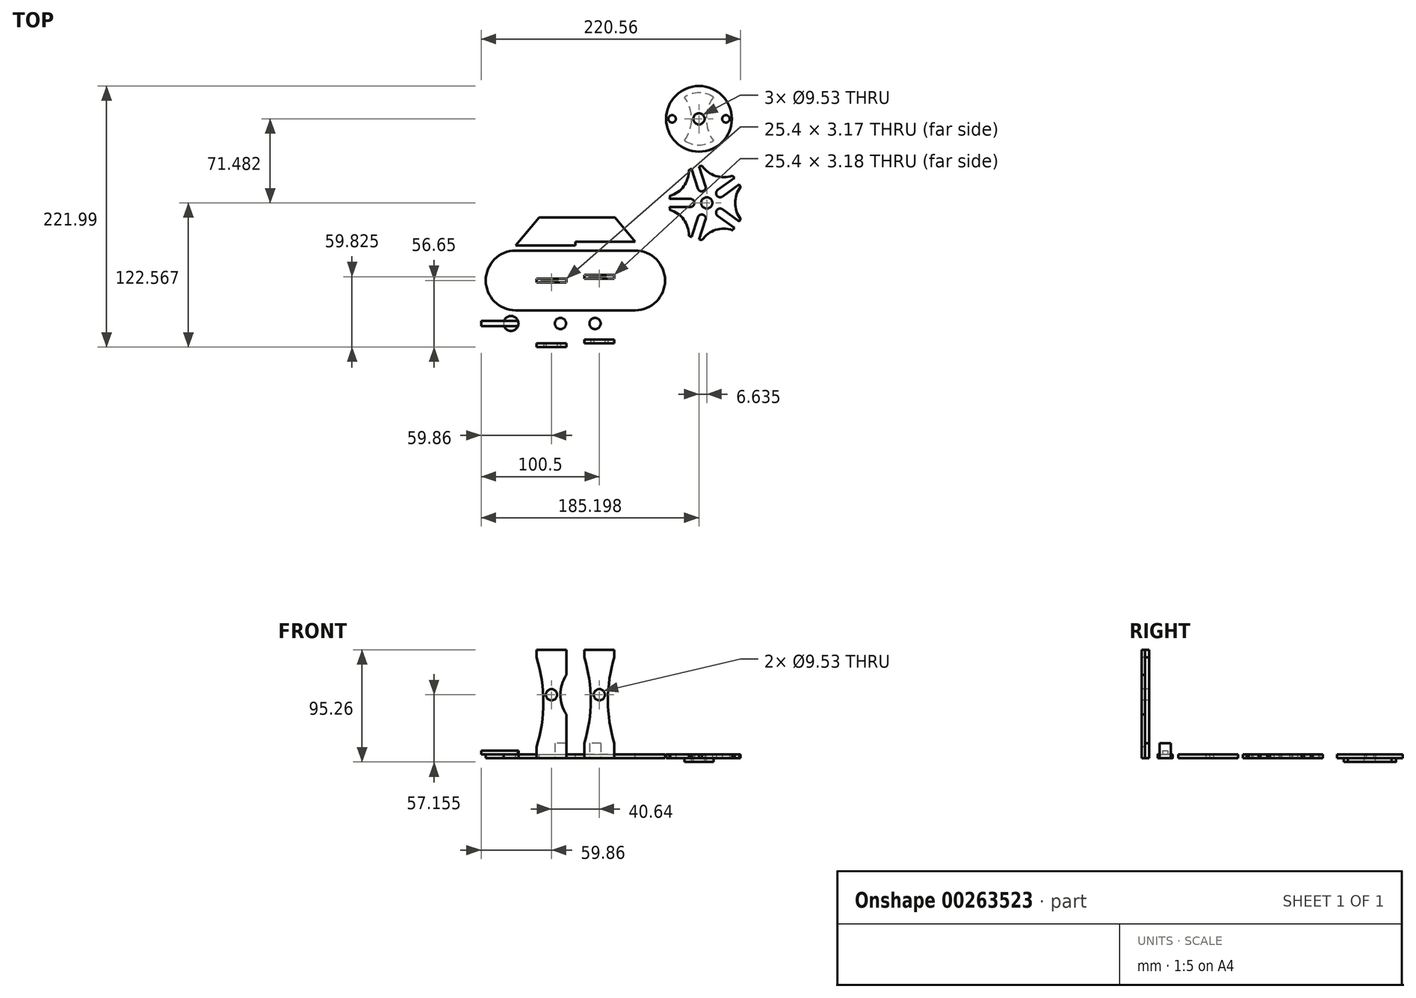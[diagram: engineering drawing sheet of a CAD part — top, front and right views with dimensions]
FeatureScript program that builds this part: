
annotation { "Feature Type Name" : "Feature", "Feature Type Description" : "" }
export const myFeature = defineFeature(function(context is Context, id is Id, definition is map)
    precondition{}
    {
        {
            var Q0;
            Q0=qCreatedBy(makeId("Top.planeOp"),FACE);
            var sketch = newSketch(context, id + "F0", { "sketchPlane" : qUnion([Q0])});
            skArc(sketch, "E0", {"start": v(-38.1, 25.4) * mm, "mid": v(-63.5, 0) * mm, "end": v(-38.1, -25.4) * mm});
            skArc(sketch, "E1", {"start": v(63.5, -25.4) * mm, "mid": v(88.9, 0) * mm, "end": v(63.5, 25.4) * mm});
            skLineSegment(sketch, "E2", {"start": v(-38.1, 25.4) * mm, "end": v(63.5, 25.4) * mm});
            skLineSegment(sketch, "E3", {"start": v(-38.1, -25.4) * mm, "end": v(63.5, -25.4) * mm});
            skSolve(sketch);
        }
        {
            var Q0;
            Q0=makeQuery(id+"F0.imprint","IMPRINT",FACE,{"disambiguationData":[TD([[makeQuery(id+"F0.imprint","IMPRINT",EDGE,{"derivedFrom":sQuery(id+"F0.wireOp",EDGE,"E0")}),1.0]])]});
            extrude(context, id + "F1", {"entities" : qUnion([Q0]), "depth" : 3.17 * mm});
        }
        {
            var Q0;
            Q0=qCreatedBy(makeId("Top.planeOp"),FACE);
            var sketch = newSketch(context, id + "F2", { "sketchPlane" : qUnion([Q0])});
            skCircle(sketch, "E4", {"center": v(117.72, 137.4) * mm, "radius": 27.94 * mm});
            skArc(sketch, "E5", {"start": v(130.02, 155.9) * mm, "mid": v(117.72, 159.62) * mm, "end": v(105.42, 155.9) * mm});
            skArc(sketch, "E6", {"start": v(146.1, 42.78) * mm, "mid": v(147, 43.67) * mm, "end": v(147.87, 44.6) * mm});
            skArc(sketch, "E7", {"start": v(120.36, 97.42) * mm, "mid": v(131.8, 88.87) * mm, "end": v(146.1, 89.05) * mm});
            skArc(sketch, "E8", {"start": v(93.16, 71.85) * mm, "mid": v(104.83, 80.1) * mm, "end": v(109.07, 93.75) * mm});
            skArc(sketch, "E9", {"start": v(109.07, 38.09) * mm, "mid": v(104.83, 51.73) * mm, "end": v(93.16, 59.98) * mm});
            skArc(sketch, "E10", {"start": v(146.1, 42.78) * mm, "mid": v(131.8, 42.97) * mm, "end": v(120.36, 34.42) * mm});
            skArc(sketch, "E11.trimOffspring", {"start": v(109.07, 38.09) * mm, "mid": v(110.2, 37.5) * mm, "end": v(111.34, 36.96) * mm});
            skArc(sketch, "E12.trimOffspring", {"start": v(153.08, 79.45) * mm, "mid": v(152.51, 80.58) * mm, "end": v(151.9, 81.7) * mm});
            skArc(sketch, "E13.trimOffspring", {"start": v(93.16, 71.85) * mm, "mid": v(92.95, 70.6) * mm, "end": v(92.79, 69.35) * mm});
            skArc(sketch, "E14.trimOffspring", {"start": v(120.36, 97.42) * mm, "mid": v(119.1, 97.23) * mm, "end": v(117.86, 97) * mm});
            skPoint(sketch, "E15", {"position": v(170.7, 65.92) * mm});
            skArc(sketch, "E16", {"start": v(153.08, 79.45) * mm, "mid": v(148.48, 65.92) * mm, "end": v(153.08, 52.39) * mm});
            skPoint(sketch, "E17", {"position": v(92.6, 65.92) * mm});
            skPoint(sketch, "E18", {"position": v(114.54, 35.72) * mm});
            skPoint(sketch, "E19", {"position": v(150.04, 47.26) * mm});
            skPoint(sketch, "E20", {"position": v(150.04, 84.58) * mm});
            skPoint(sketch, "E21", {"position": v(114.54, 96.11) * mm});
            skCircle(sketch, "E22", {"center": v(94.86, 137.4) * mm, "radius": 3.18 * mm});
            skPoint(sketch, "E23", {"position": v(110.38, 65.92) * mm});
            skArc(sketch, "E24.trimOffspring", {"start": v(92.79, 62.49) * mm, "mid": v(92.95, 61.23) * mm, "end": v(93.16, 59.98) * mm});
            skArc(sketch, "E25.trimOffspring", {"start": v(111.34, 94.88) * mm, "mid": v(110.2, 94.33) * mm, "end": v(109.07, 93.75) * mm});
            skArc(sketch, "E26.trimOffspring", {"start": v(147.87, 87.24) * mm, "mid": v(147, 88.17) * mm, "end": v(146.1, 89.05) * mm});
            skArc(sketch, "E27.trimOffspring", {"start": v(151.9, 50.14) * mm, "mid": v(152.51, 51.25) * mm, "end": v(153.08, 52.39) * mm});
            skArc(sketch, "E28.trimOffspring", {"start": v(117.86, 34.84) * mm, "mid": v(119.1, 34.6) * mm, "end": v(120.36, 34.42) * mm});
            skCircle(sketch, "E29", {"center": v(124.35, 65.92) * mm, "radius": 4.76 * mm});
            skCircle(sketch, "E30", {"center": v(117.72, 137.4) * mm, "radius": 4.76 * mm});
            skCircle(sketch, "E31", {"center": v(140.58, 137.4) * mm, "radius": 3.18 * mm});
            skArc(sketch, "E32", {"start": v(130.02, 155.9) * mm, "mid": v(124.07, 137.4) * mm, "end": v(130.02, 118.9) * mm});
            skArc(sketch, "E33", {"start": v(105.42, 118.9) * mm, "mid": v(111.37, 137.4) * mm, "end": v(105.42, 155.9) * mm});
            skArc(sketch, "E34.trimOffspring", {"start": v(105.42, 118.9) * mm, "mid": v(117.72, 115.17) * mm, "end": v(130.02, 118.9) * mm});
            skPoint(sketch, "E35.end.orphan", {"position": v(110.38, 62.49) * mm});
            skPoint(sketch, "E35.start.orphan", {"position": v(110.38, 69.35) * mm});
            skPoint(sketch, "E36", {"position": v(93.16, 65.92) * mm});
            skArc(sketch, "E37", {"start": v(110.38, 69.35) * mm, "mid": v(113.81, 65.92) * mm, "end": v(110.38, 62.49) * mm});
            skLineSegment(sketch, "E38", {"start": v(110.38, 69.35) * mm, "end": v(92.79, 69.35) * mm});
            skLineSegment(sketch, "E39", {"start": v(110.38, 62.49) * mm, "end": v(92.79, 62.49) * mm});
            skLineSegment(sketch, "E40.1.0", {"start": v(123.3, 80.26) * mm, "end": v(117.86, 97) * mm});
            skArc(sketch, "E40.1.1", {"start": v(123.3, 80.26) * mm, "mid": v(121.1, 75.94) * mm, "end": v(116.78, 78.14) * mm});
            skLineSegment(sketch, "E40.1.2", {"start": v(116.78, 78.14) * mm, "end": v(111.34, 94.88) * mm});
            skLineSegment(sketch, "E40.2.0", {"start": v(137.67, 71.35) * mm, "end": v(151.9, 81.7) * mm});
            skArc(sketch, "E40.2.1", {"start": v(137.67, 71.35) * mm, "mid": v(132.88, 72.11) * mm, "end": v(133.64, 76.9) * mm});
            skLineSegment(sketch, "E40.2.2", {"start": v(133.64, 76.9) * mm, "end": v(147.87, 87.24) * mm});
            skLineSegment(sketch, "E40.3.0", {"start": v(133.64, 54.93) * mm, "end": v(147.87, 44.6) * mm});
            skArc(sketch, "E40.3.1", {"start": v(133.64, 54.93) * mm, "mid": v(132.88, 59.72) * mm, "end": v(137.67, 60.48) * mm});
            skLineSegment(sketch, "E40.3.2", {"start": v(137.67, 60.48) * mm, "end": v(151.9, 50.14) * mm});
            skLineSegment(sketch, "E40.4.0", {"start": v(116.78, 53.7) * mm, "end": v(111.34, 36.96) * mm});
            skArc(sketch, "E40.4.1", {"start": v(116.78, 53.7) * mm, "mid": v(121.1, 55.9) * mm, "end": v(123.3, 51.57) * mm});
            skLineSegment(sketch, "E40.4.2", {"start": v(123.3, 51.57) * mm, "end": v(117.86, 34.84) * mm});
            skLineSegment(sketch, "E40.anchor1", {"start": v(124.35, 65.92) * mm, "end": v(92.79, 69.35) * mm, "construction": true});
            skLineSegment(sketch, "E40.anchor2", {"start": v(124.35, 65.92) * mm, "end": v(111.34, 36.96) * mm, "construction": true});
            skSolve(sketch);
        }
        {
            var Q0;
            Q0=makeQuery(id+"F1.opExtrude","CAP_FACE",FACE,{"disambiguationData":[OSD([sQuery(id+"F0.wireOp",EDGE,"E0"),sQuery(id+"F0.wireOp",EDGE,"E1"),sQuery(id+"F0.wireOp",EDGE,"E2"),sQuery(id+"F0.wireOp",EDGE,"E3")])],"isStart":false});
            var sketch = newSketch(context, id + "F3", { "sketchPlane" : qUnion([Q0])});
            skSolve(sketch);
        }
        {
            var Q0;
            Q0=makeQuery(id+"F2.imprint","IMPRINT",FACE,{"disambiguationData":[TD([[makeQuery(id+"F2.imprint","IMPRINT",EDGE,{"derivedFrom":sQuery(id+"F2.wireOp",EDGE,"E6")}),1.0]])]});
            extrude(context, id + "F4", {"entities" : qUnion([Q0]), "depth" : 3.17 * mm});
        }
        {
            var Q0;
            Q0=makeQuery(id+"F2.imprint","IMPRINT",FACE,{"disambiguationData":[TD([[makeQuery(id+"F2.imprint","IMPRINT",EDGE,{"derivedFrom":sQuery(id+"F2.wireOp",EDGE,"E5")}),1.0]])]});
            extrude(context, id + "F5", {"entities" : qUnion([Q0]), "depth" : 3.17 * mm});
        }
        {
            var Q0;
            Q0=makeQuery(id+"F2.imprint","IMPRINT",FACE,{"disambiguationData":[TD([[makeQuery(id+"F2.imprint","IMPRINT",EDGE,{"derivedFrom":sQuery(id+"F2.wireOp",EDGE,"E4")}),1.0]])]});
            extrude(context, id + "F6", {"entities" : qUnion([Q0]), "operationType" : NewBodyOperationType.ADD, "depth" : 3.17 * mm});
        }
        {
            var Q0;
            Q0=makeQuery(id+"F3.imprint","IMPRINT",FACE,{"disambiguationData":[TD([[makeQuery(id+"F3.imprint","IMPRINT",EDGE,{"derivedFrom":makeQuery(id+"F1.opExtrude","CAP_EDGE",EDGE,{"disambiguationData":[OSD([sQuery(id+"F0.wireOp",EDGE,"E0")])],"isStart":false})}),1.0]])]});
            var sketch = newSketch(context, id + "F7", { "sketchPlane" : qUnion([Q0])});
            skPoint(sketch, "E41", {"position": v(-38.1, 53.47) * mm});
            skPoint(sketch, "E42", {"position": v(63.5, 53.47) * mm});
            skLineSegment(sketch, "E43", {"start": v(-18.12, 53.47) * mm, "end": v(46.18, 53.47) * mm});
            skPoint(sketch, "E44", {"position": v(12.7, 53.47) * mm});
            skPoint(sketch, "E45", {"position": v(12.7, 0) * mm});
            skPoint(sketch, "E46", {"position": v(-7.62, 0) * mm});
            skLineSegment(sketch, "E47.bottom", {"start": v(-20.32, -1.59) * mm, "end": v(5.08, -1.59) * mm});
            skLineSegment(sketch, "E47.left", {"start": v(-20.32, -1.59) * mm, "end": v(-20.32, 1.59) * mm});
            skLineSegment(sketch, "E47.right", {"start": v(5.08, -1.59) * mm, "end": v(5.08, 1.59) * mm});
            skLineSegment(sketch, "E48.top", {"start": v(20.32, 1.59) * mm, "end": v(45.72, 1.59) * mm});
            skLineSegment(sketch, "E49", {"start": v(20.32, 1.59) * mm, "end": v(20.32, 4.76) * mm});
            skLineSegment(sketch, "E50", {"start": v(20.32, 4.76) * mm, "end": v(45.72, 4.76) * mm});
            skLineSegment(sketch, "E51", {"start": v(45.72, 4.76) * mm, "end": v(45.72, 1.59) * mm});
            skPoint(sketch, "E52", {"position": v(33.02, 0) * mm});
            skLineSegment(sketch, "E53", {"start": v(-20.32, 1.59) * mm, "end": v(5.08, 1.59) * mm});
            skLineSegment(sketch, "E54", {"start": v(5.08, -53.47) * mm, "end": v(5.08, -56.65) * mm});
            skLineSegment(sketch, "E55", {"start": v(5.08, -56.65) * mm, "end": v(-20.32, -56.65) * mm});
            skLineSegment(sketch, "E56", {"start": v(-20.32, -56.65) * mm, "end": v(-20.32, -53.47) * mm});
            skLineSegment(sketch, "E57", {"start": v(-20.32, -53.47) * mm, "end": v(5.08, -53.47) * mm});
            skLineSegment(sketch, "E58", {"start": v(20.32, -53.47) * mm, "end": v(20.32, -50.3) * mm});
            skLineSegment(sketch, "E59", {"start": v(20.32, -50.3) * mm, "end": v(45.72, -50.3) * mm});
            skLineSegment(sketch, "E60", {"start": v(45.72, -50.3) * mm, "end": v(45.72, -53.47) * mm});
            skLineSegment(sketch, "E61", {"start": v(45.72, -53.47) * mm, "end": v(20.32, -53.47) * mm});
            skPoint(sketch, "E62", {"position": v(33.02, 4.76) * mm});
            skLineSegment(sketch, "E63", {"start": v(-38.1, 29.66) * mm, "end": v(12.7, 29.66) * mm});
            skLineSegment(sketch, "E64", {"start": v(63.5, 32.83) * mm, "end": v(12.7, 32.83) * mm});
            skLineSegment(sketch, "E65", {"start": v(12.7, 29.66) * mm, "end": v(12.7, 32.83) * mm});
            skLineSegment(sketch, "E66", {"start": v(-38.1, 29.66) * mm, "end": v(-18.12, 53.47) * mm});
            skLineSegment(sketch, "E67", {"start": v(63.5, 32.83) * mm, "end": v(46.18, 53.47) * mm});
            skSolve(sketch);
        }
        {
            var Q0;
            Q0=makeQuery(id+"F2.imprint","IMPRINT",FACE,{"disambiguationData":[TD([[makeQuery(id+"F2.imprint","IMPRINT",EDGE,{"derivedFrom":sQuery(id+"F2.wireOp",EDGE,"E6")}),1.0]])]});
            extrude(context, id + "F8", {"entities" : qUnion([Q0]), "operationType" : NewBodyOperationType.ADD, "depth" : 3.17 * mm});
        }
        {
            var Q0;
            Q0=makeQuery(id+"F7.imprint","IMPRINT",FACE,{"disambiguationData":[TD([[makeQuery(id+"F7.imprint","IMPRINT",EDGE,{"derivedFrom":sQuery(id+"F7.wireOp",EDGE,"E47.bottom")}),1.0]])]});
            extrude(context, id + "F9", {"entities" : qUnion([Q0]), "operationType" : NewBodyOperationType.REMOVE, "oppositeDirection" : true, "depth" : 3.17 * mm});
        }
        {
            var Q0;
            Q0=makeQuery(id+"F7.imprint","IMPRINT",FACE,{"disambiguationData":[TD([[makeQuery(id+"F7.imprint","IMPRINT",EDGE,{"derivedFrom":sQuery(id+"F7.wireOp",EDGE,"E48.top")}),1.0]])]});
            extrude(context, id + "F10", {"entities" : qUnion([Q0]), "operationType" : NewBodyOperationType.REMOVE, "oppositeDirection" : true, "depth" : 3.17 * mm});
        }
        {
            var Q0;
            Q0=makeQuery(id+"F7.imprint","IMPRINT",FACE,{"disambiguationData":[TD([[makeQuery(id+"F7.imprint","IMPRINT",EDGE,{"derivedFrom":sQuery(id+"F7.wireOp",EDGE,"E54")}),-1.0]])]});
            var Q1;
            Q1=makeQuery(id+"F7.imprint","IMPRINT",FACE,{"disambiguationData":[TD([[makeQuery(id+"F7.imprint","IMPRINT",EDGE,{"derivedFrom":sQuery(id+"F7.wireOp",EDGE,"E58")}),-1.0]])]});
            extrude(context, id + "F11", {"entities" : qUnion([Q0, Q1]), "depth" : 88.9 * mm});
        }
        {
            var Q0;
            Q0=makeQuery(id+"F11.opExtrude","SWEPT_FACE",FACE,{"disambiguationData":[OSD([sQuery(id+"F7.wireOp",EDGE,"E61")])]});
            var sketch = newSketch(context, id + "F12", { "sketchPlane" : qUnion([Q0])});
            skLineSegment(sketch, "E68", {"start": v(20.32, 6.35) * mm, "end": v(20.32, 12.7) * mm});
            skLineSegment(sketch, "E69", {"start": v(45.72, 12.7) * mm, "end": v(45.72, 6.35) * mm});
            skLineSegment(sketch, "E70", {"start": v(20.32, 92.08) * mm, "end": v(20.32, 85.73) * mm});
            skLineSegment(sketch, "E71", {"start": v(45.72, 92.08) * mm, "end": v(45.72, 85.73) * mm});
            skArc(sketch, "E72", {"start": v(20.32, 12.7) * mm, "mid": v(25.68, 49.21) * mm, "end": v(20.32, 85.73) * mm});
            skArc(sketch, "E73", {"start": v(45.72, 85.73) * mm, "mid": v(40.36, 49.21) * mm, "end": v(45.72, 12.7) * mm});
            skPoint(sketch, "E74", {"position": v(33.02, 92.08) * mm});
            skPoint(sketch, "E75", {"position": v(33.02, 53.98) * mm});
            skCircle(sketch, "E76", {"center": v(33.02, 53.98) * mm, "radius": 4.76 * mm});
            skSolve(sketch);
        }
        {
            var Q0;
            Q0=makeQuery(id+"F7.imprint","IMPRINT",FACE,{"disambiguationData":[TD([[makeQuery(id+"F7.imprint","IMPRINT",EDGE,{"derivedFrom":sQuery(id+"F7.wireOp",EDGE,"E54")}),-1.0]])]});
            extrude(context, id + "F13", {"entities" : qUnion([Q0]), "operationType" : NewBodyOperationType.ADD, "oppositeDirection" : true, "depth" : 3.17 * mm});
        }
        {
            var Q0;
            Q0=makeQuery(id+"F7.imprint","IMPRINT",FACE,{"disambiguationData":[TD([[makeQuery(id+"F7.imprint","IMPRINT",EDGE,{"derivedFrom":sQuery(id+"F7.wireOp",EDGE,"E58")}),-1.0]])]});
            extrude(context, id + "F14", {"entities" : qUnion([Q0]), "operationType" : NewBodyOperationType.ADD, "oppositeDirection" : true, "depth" : 3.17 * mm});
        }
        {
            var Q0;
            {var subQ0=sQuery(id+"F7.wireOp",EDGE,"E55");Q0=makeQuery(id+"F13.boolean.opBoolean","MERGE",FACE,{"derivedFrom":[makeQuery(id+"F11.opExtrude","SWEPT_FACE",FACE,{"disambiguationData":[OSD([subQ0])]}),makeQuery(id+"F13.opExtrude","SWEPT_FACE",FACE,{"disambiguationData":[OSD([subQ0])]})]});}
            var sketch = newSketch(context, id + "F15", { "sketchPlane" : qUnion([Q0])});
            skPoint(sketch, "E77", {"position": v(-7.62, 92.08) * mm});
            skPoint(sketch, "E78", {"position": v(-7.62, 53.98) * mm});
            skPoint(sketch, "E79", {"position": v(30.48, 53.98) * mm});
            skArc(sketch, "E80", {"start": v(5.08, 70.82) * mm, "mid": v(0, 53.98) * mm, "end": v(5.08, 37.13) * mm});
            skLineSegment(sketch, "E81", {"start": v(-20.32, 3.18) * mm, "end": v(-20.32, 9.53) * mm});
            skLineSegment(sketch, "E82", {"start": v(-20.32, 92.08) * mm, "end": v(-20.32, 85.73) * mm});
            skArc(sketch, "E83", {"start": v(-20.32, 9.53) * mm, "mid": v(-14.47, 47.63) * mm, "end": v(-20.32, 85.72) * mm});
            skCircle(sketch, "E84", {"center": v(-7.62, 53.98) * mm, "radius": 4.76 * mm});
            skSolve(sketch);
        }
        {
            var Q0;
            {var subQ0=sQuery(id+"F15.wireOp",EDGE,"E80");Q0=makeQuery(id+"F15.imprint","IMPRINT",FACE,{"disambiguationData":[TD([[makeQuery(id+"F15.imprint","IMPRINT",EDGE,{"derivedFrom":subQ0}),1.0]])]});}
            var Q1;
            {var subQ0=sQuery(id+"F15.wireOp",EDGE,"E83");Q1=makeQuery(id+"F15.imprint","IMPRINT",FACE,{"disambiguationData":[TD([[makeQuery(id+"F15.imprint","IMPRINT",EDGE,{"derivedFrom":subQ0}),1.0]])]});}
            extrude(context, id + "F16", {"entities" : qUnion([Q0, Q1]), "operationType" : NewBodyOperationType.REMOVE, "oppositeDirection" : true, "depth" : 3.17 * mm});
        }
        {
            var Q0;
            {var subQ0=sQuery(id+"F12.wireOp",EDGE,"E72");Q0=makeQuery(id+"F12.imprint","IMPRINT",FACE,{"disambiguationData":[TD([[makeQuery(id+"F12.imprint","IMPRINT",EDGE,{"derivedFrom":subQ0}),1.0]])]});}
            var Q1;
            {var subQ0=sQuery(id+"F12.wireOp",EDGE,"E73");Q1=makeQuery(id+"F12.imprint","IMPRINT",FACE,{"disambiguationData":[TD([[makeQuery(id+"F12.imprint","IMPRINT",EDGE,{"derivedFrom":subQ0}),1.0]])]});}
            extrude(context, id + "F17", {"entities" : qUnion([Q0, Q1]), "operationType" : NewBodyOperationType.REMOVE, "oppositeDirection" : true, "depth" : 3.17 * mm});
        }
        {
            var Q0;
            Q0=makeQuery(id+"F12.imprint","IMPRINT",FACE,{"disambiguationData":[TD([[makeQuery(id+"F12.imprint","IMPRINT",EDGE,{"derivedFrom":sQuery(id+"F12.wireOp",EDGE,"E76")}),1.0]])]});
            extrude(context, id + "F18", {"entities" : qUnion([Q0]), "operationType" : NewBodyOperationType.REMOVE, "oppositeDirection" : true, "depth" : 3.17 * mm});
        }
        {
            var Q0;
            Q0=makeQuery(id+"F15.imprint","IMPRINT",FACE,{"disambiguationData":[TD([[makeQuery(id+"F15.imprint","IMPRINT",EDGE,{"derivedFrom":sQuery(id+"F15.wireOp",EDGE,"E84")}),1.0]])]});
            extrude(context, id + "F19", {"entities" : qUnion([Q0]), "operationType" : NewBodyOperationType.REMOVE, "oppositeDirection" : true, "depth" : 3.17 * mm});
        }
        {
            var Q0;
            Q0=makeQuery(id+"F2.imprint","IMPRINT",FACE,{"disambiguationData":[TD([[makeQuery(id+"F2.imprint","IMPRINT",EDGE,{"derivedFrom":sQuery(id+"F2.wireOp",EDGE,"E5")}),1.0]])]});
            extrude(context, id + "F20", {"entities" : qUnion([Q0]), "oppositeDirection" : true, "depth" : 3.17 * mm});
        }
        {
            var Q0;
            Q0=qCreatedBy(makeId("Top.planeOp"),FACE);
            var sketch = newSketch(context, id + "F21", { "sketchPlane" : qUnion([Q0])});
            skPoint(sketch, "E85", {"position": v(0, -36.61) * mm});
            skPoint(sketch, "E86", {"position": v(29.4, -36.61) * mm});
            skCircle(sketch, "E87", {"center": v(0, -36.61) * mm, "radius": 4.76 * mm});
            skCircle(sketch, "E88", {"center": v(29.4, -36.61) * mm, "radius": 4.76 * mm});
            skPoint(sketch, "E89", {"position": v(-42.08, -36.61) * mm});
            skCircle(sketch, "E90", {"center": v(-42.08, -36.61) * mm, "radius": 6.35 * mm});
            skSolve(sketch);
        }
        {
            var Q0;
            Q0=makeQuery(id+"F21.imprint","IMPRINT",FACE,{"disambiguationData":[TD([[makeQuery(id+"F21.imprint","IMPRINT",EDGE,{"derivedFrom":sQuery(id+"F21.wireOp",EDGE,"E88")}),1.0]])]});
            extrude(context, id + "F22", {"entities" : qUnion([Q0]), "depth" : 12.7 * mm});
        }
        {
            var Q0;
            Q0=makeQuery(id+"F21.imprint","IMPRINT",FACE,{"disambiguationData":[TD([[makeQuery(id+"F21.imprint","IMPRINT",EDGE,{"derivedFrom":sQuery(id+"F21.wireOp",EDGE,"E90")}),1.0]])]});
            extrude(context, id + "F23", {"entities" : qUnion([Q0]), "depth" : 3.17 * mm});
        }
        {
            var Q0;
            Q0=makeQuery(id+"F23.opExtrude","CAP_FACE",FACE,{"disambiguationData":[OSD([sQuery(id+"F21.wireOp",EDGE,"E90")])],"isStart":false});
            var sketch = newSketch(context, id + "F24", { "sketchPlane" : qUnion([Q0])});
            skLineSegment(sketch, "E91.bottom", {"start": v(-67.48, -38.84) * mm, "end": v(-16.68, -38.84) * mm});
            skLineSegment(sketch, "E91.top", {"start": v(-67.48, -34.4) * mm, "end": v(-16.68, -34.4) * mm});
            skLineSegment(sketch, "E91.left", {"start": v(-67.48, -38.84) * mm, "end": v(-67.48, -34.4) * mm});
            skLineSegment(sketch, "E91.right", {"start": v(-16.68, -38.84) * mm, "end": v(-16.68, -34.4) * mm});
            skPoint(sketch, "E91.middle", {"position": v(-42.08, -36.61) * mm});
            skSolve(sketch);
        }
        {
            var Q0;
            {var subQ0=sQuery(id+"F24.wireOp",EDGE,"E91.left");Q0=makeQuery(id+"F24.imprint","IMPRINT",FACE,{"disambiguationData":[TD([[makeQuery(id+"F24.imprint","IMPRINT",EDGE,{"derivedFrom":subQ0}),-1.0]])]});}
            var Q1;
            {var subQ0=sQuery(id+"F24.wireOp",EDGE,"E91.bottom");var subQ1=makeQuery(id+"F23.opExtrude","CAP_EDGE",EDGE,{"disambiguationData":[OSD([sQuery(id+"F21.wireOp",EDGE,"E90")])],"isStart":false});var subQ2=makeQuery(id+"F24.imprint","INTERSECT",VERTEX,{"disambiguationData":[OD(0.0)],"derivedFrom":[subQ1,subQ0]});Q1=makeQuery(id+"F24.imprint","IMPRINT",FACE,{"disambiguationData":[TD([[makeQuery(id+"F24.imprint","IMPRINT",EDGE,{"disambiguationData":[TD([[subQ2,-1.0]])],"derivedFrom":subQ0}),1.0]])]});}
            extrude(context, id + "F25", {"entities" : qUnion([Q0, Q1]), "depth" : 3.17 * mm});
        }
        {
            var Q0;
            Q0=makeQuery(id+"F21.imprint","IMPRINT",FACE,{"disambiguationData":[TD([[makeQuery(id+"F21.imprint","IMPRINT",EDGE,{"derivedFrom":sQuery(id+"F21.wireOp",EDGE,"E87")}),1.0]])]});
            extrude(context, id + "F26", {"entities" : qUnion([Q0]), "depth" : 12.7 * mm});
        }
        {
            var Q0;
            Q0=makeQuery(id+"F7.imprint","IMPRINT",FACE,{"disambiguationData":[TD([[makeQuery(id+"F7.imprint","IMPRINT",EDGE,{"derivedFrom":sQuery(id+"F7.wireOp",EDGE,"E43")}),-1.0]])]});
            extrude(context, id + "F27", {"entities" : qUnion([Q0]), "oppositeDirection" : true, "depth" : 3.17 * mm});
        }
    });
